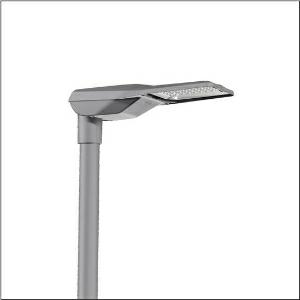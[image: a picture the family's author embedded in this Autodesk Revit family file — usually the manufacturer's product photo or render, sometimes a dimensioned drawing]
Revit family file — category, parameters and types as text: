
# Revit family: streetlight_sl_21_iq_mini___st1_0a_5xe2d41g08jb_4fff
name_source: partatom
category: Lighting Fixtures
units: mm (PartAtom-declared; Revit-internal decimal feet)

## family parameters
Cut with Voids When Loaded = No
Host = Face
Light Source = No
Part Type = Normal
Room Calculation Point = No
Round Connector Dimension = Use Diameter
Shared = No

## types (1)
- --- (1 x LED, 11290 lm, 71.6 W, 4000K)
    Apparent Load = 72 VA
    CIE Flux Codes = 40 73 97 100 100
    Color Rendering = 70
    Color Temperature = 4000K
    Default Elevation = 1800 mm
    Description = Streetlight SL 21 iQ mini, mast luminaire, primary light control with lens, of PMMA, primary optical cover: cover, of toughened safety glass, transparent, light distribution: ST1.0a, light emission: direct distribution, primary light characteristic: asymmetric, installation type: post-top, side-entry, LED, High Power LED, rated luminous flux: 11.290lm, luminous efficacy: 158lm/W, light colour: 740, colour temperature: 4000K, control gear: iQ Street-Remote, control: Street-Remote, Auto-Match, Temp-Guard, Lumen-Switch, Night-Set, Smart-Wire, Light-Fading, Desk-Remote (wireless, voltage-free reading and setting of iQ features in the workshop via application-optimized NFC function/RFID function), optimised constant luminous flux control (CLO 2.0), pre-setting: linear dimming characteristic, mains connection: 220..240V, AC, 50/60Hz, start of lifetime: 72W, end of service life: 75W, reduction: 33W, luminaire housing, of diecast aluminium, powder-coated, Siteco® metallic grey (DB 702S), corrosivity category C5 mid according to DIN EN ISO 12944, please order mast flange separately, inclination adjustable: 0°, 5°, 10°, 15°, sealing non-destructively replaceable, multi-level sealing system, length: 628mm, width: 235mm, height: 110mm, mast flange for spigot size: 42mm (side-entry): 5XC10008XM4, 60/48mm (side-entry/post-top): 5XC10108XM2, 76/60mm (side-entry/post-top): 5XC10108XM1, mounting height: 4..8m, protection rating (complete): IP66, insulation class (complete): insulation class II (safety insulation), certification: CE, ENEC, ENEC+, VDE, impact resistance: IK10, permissible operating ambient temperature for outdoor applications: -40..+50°C, standard-compliant lighting for roads and squares, packaging unit: 1 piece

Light Distribution: ST1.0a
    Height = 110 mm
    Lamp = 1 x LED
    Lamp Light Flux = 11290 lm
    Lamp Power = 71.6 W
    Lamp count = 1
    Length = 625 mm
    Luminous efficacy = 158 lm/W
    Manufacturer = Siteco
    ModVariant = No
    Model = 5XE2D41G08JB
    Number of Poles = 1
    OnlyDefault = Yes
    Power Factor = 1
    Product Name = Streetlight SL 21 iQ mini | ST1.0a
    Product group = mast luminaire | pylon top
    ProductGroupID = 6100
    Protection Class = Protection class II
    Protection Degree = IP 66
    RLX_Detail_Level = 1
    RLX_Emergency_Light_Flux = 0 lm
    RLX_Emergency_Type = 0
    RLX_Emergency_Type_DB = No
    RlxData = <blob elided: 26321 chars, md5=5d4ed184>
    Socket = socket
    Standby Power = 0 W
    System Light Flux = 11290 lm
    System Power = 72 W
    Type Comments = factory setting: luminous flux: 100 % | dim-lin: 254 | 746 mA
    Type Image = l_1003519.jpg
    URL = http://relux.com
    VarID = @adj_192551
    Voltage = 0 V
    Weight = 0.00 kg
    Width = 234 mm

## geometry (parser evidence)
native form markers: Blend x4, Sweep x10
no freeform markers — native parametric forms only
